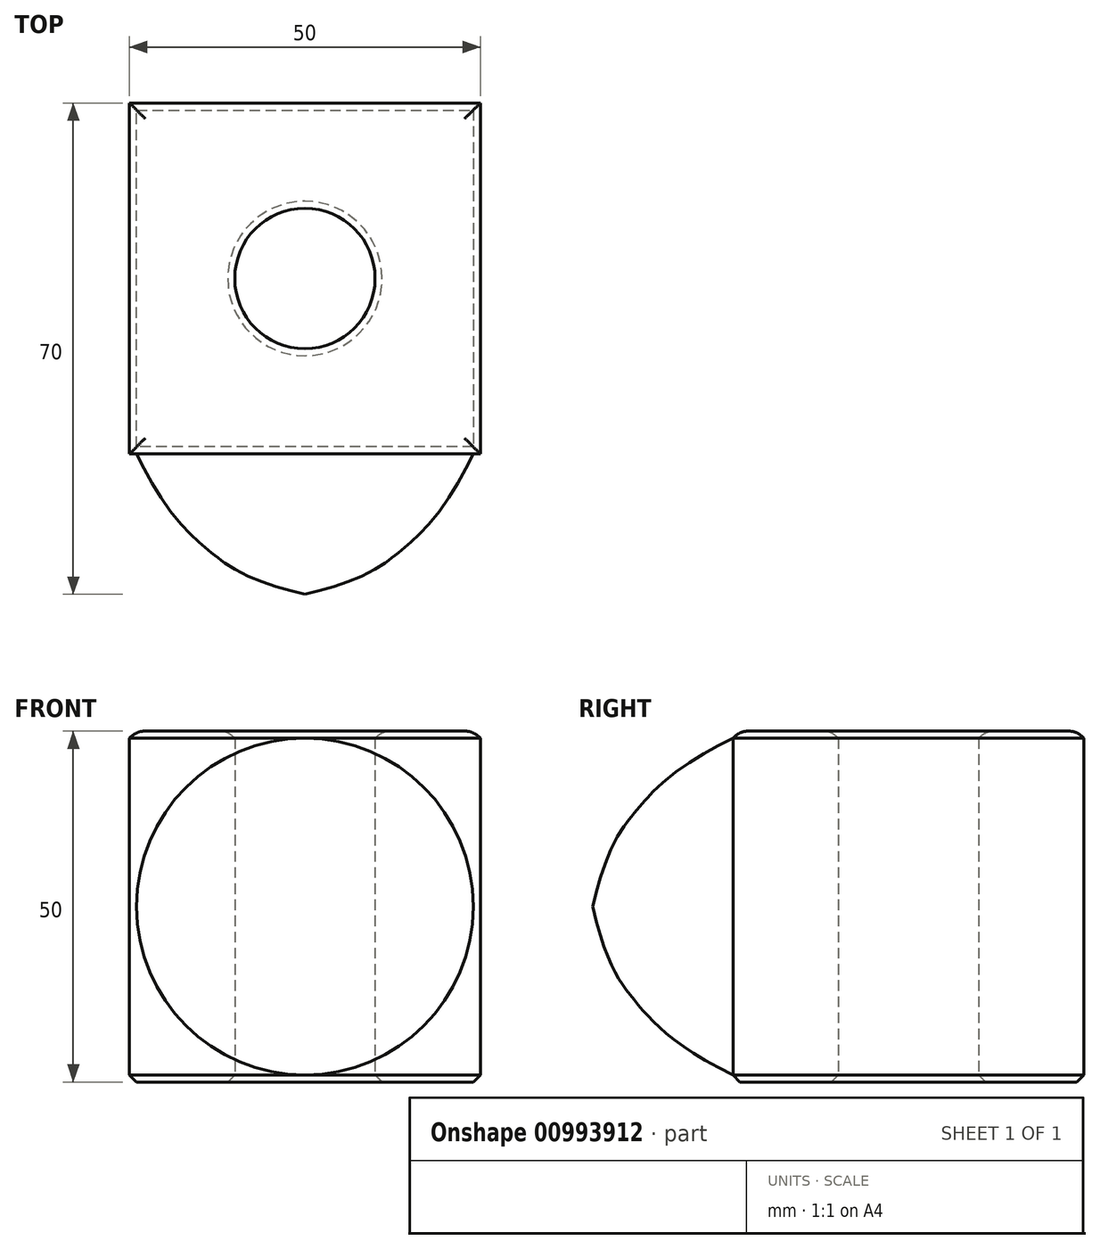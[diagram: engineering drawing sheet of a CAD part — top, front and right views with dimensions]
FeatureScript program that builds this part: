
annotation { "Feature Type Name" : "Feature", "Feature Type Description" : "" }
export const myFeature = defineFeature(function(context is Context, id is Id, definition is map)
    precondition{}
    {
        {
            var Q0;
            Q0=qCreatedBy(makeId("Top.planeOp"),FACE);
            var sketch = newSketch(context, id + "F0", { "sketchPlane" : qUnion([Q0])});
            skLineSegment(sketch, "E0.bottom", {"start": v(25, 25) * mm, "end": v(-25, 25) * mm});
            skLineSegment(sketch, "E0.top", {"start": v(25, -25) * mm, "end": v(-25, -25) * mm});
            skLineSegment(sketch, "E0.left", {"start": v(25, 25) * mm, "end": v(25, -25) * mm});
            skLineSegment(sketch, "E0.right", {"start": v(-25, 25) * mm, "end": v(-25, -25) * mm});
            skPoint(sketch, "E0.middle", {"position": v(0, 0) * mm});
            skSolve(sketch);
        }
        {
            var Q0;
            Q0=makeQuery(id+"F0.imprint","IMPRINT",FACE,{"disambiguationData":[TD([[makeQuery(id+"F0.imprint","IMPRINT",EDGE,{"derivedFrom":sQuery(id+"F0.wireOp",EDGE,"E0.bottom")}),1.0]])]});
            extrude(context, id + "F1", {"entities" : qUnion([Q0]), "depth" : 50 * mm, "offsetDistance" : 25 * mm});
        }
        {
            var Q0;
            Q0=qCreatedBy(makeId("Top.planeOp"),FACE);
            var sketch = newSketch(context, id + "F2", { "sketchPlane" : qUnion([Q0])});
            skCircle(sketch, "E1", {"center": v(0, 0) * mm, "radius": 10 * mm});
            skSolve(sketch);
        }
        {
            var Q0;
            Q0 = qSketchRegion(id + "F2", true);
            var Q1;
            Q1=makeQuery(id+"F1.opExtrude","CAP_FACE",FACE,{"disambiguationData":[OSD([sQuery(id+"F0.wireOp",EDGE,"E0.bottom"),sQuery(id+"F0.wireOp",EDGE,"E0.top"),sQuery(id+"F0.wireOp",EDGE,"E0.left"),sQuery(id+"F0.wireOp",EDGE,"E0.right")])],"isStart":false});
            extrude(context, id + "F3", {"entities" : qUnion([Q0, Q1]), "operationType" : NewBodyOperationType.REMOVE, "endBound" : BoundingType.THROUGH_ALL, "depth" : 20 * mm, "offsetDistance" : 25 * mm});
        }
        {
            var Q0;
            Q0=makeQuery(id+"F1.opExtrude","CAP_FACE",FACE,{"disambiguationData":[OSD([sQuery(id+"F0.wireOp",EDGE,"E0.bottom"),sQuery(id+"F0.wireOp",EDGE,"E0.top"),sQuery(id+"F0.wireOp",EDGE,"E0.left"),sQuery(id+"F0.wireOp",EDGE,"E0.right")])],"isStart":true});
            var Q1;
            Q1=makeQuery(id+"F1.opExtrude","CAP_FACE",FACE,{"disambiguationData":[OSD([sQuery(id+"F0.wireOp",EDGE,"E0.bottom"),sQuery(id+"F0.wireOp",EDGE,"E0.top"),sQuery(id+"F0.wireOp",EDGE,"E0.left"),sQuery(id+"F0.wireOp",EDGE,"E0.right")])],"isStart":false});
            chamfer(context, id + "F4", {"entities" : qUnion([Q0, Q1]), "width" : 1 * mm, "tangentPropagation" : true});
        }
        {
            var Q0;
            Q0=makeQuery(id+"F1.opExtrude","CAP_FACE",FACE,{"disambiguationData":[OSD([sQuery(id+"F0.wireOp",EDGE,"E0.bottom"),sQuery(id+"F0.wireOp",EDGE,"E0.top"),sQuery(id+"F0.wireOp",EDGE,"E0.left"),sQuery(id+"F0.wireOp",EDGE,"E0.right")])],"isStart":false});
            fillet(context, id + "F5", {"entities" : qUnion([Q0]), "radius" : 3 * mm, "tangentPropagation" : true, "rho" : 0.5, "crossSection" : FilletCrossSection.CONIC, "allowEdgeOverflow" : false});
        }
        {
            var Q0;
            Q0=qCreatedBy(makeId("Right.planeOp"),FACE);
            var sketch = newSketch(context, id + "F6", { "sketchPlane" : qUnion([Q0])});
            skLineSegment(sketch, "E2.0", {"start": v(-25, 25) * mm, "end": v(-25, 1) * mm});
            skLineSegment(sketch, "E3", {"start": v(-25, 25) * mm, "end": v(-45, 25) * mm});
            skFitSpline(sketch, "E4", {"points": [v(-45, 25) * mm, v(-39.14, 11.78) * mm, v(-25, 1) * mm], "startDerivative": vector(13, -53.55) * mm, "endDerivative": vector(50.8, -24.84) * mm});
            skPoint(sketch, "E5.orphan", {"position": v(-25, 49) * mm});
            skSolve(sketch);
        }
        {
            var Q0;
            Q0=makeQuery(id+"F6.imprint","IMPRINT",FACE,{"disambiguationData":[TD([[makeQuery(id+"F6.imprint","IMPRINT",EDGE,{"derivedFrom":sQuery(id+"F6.wireOp",EDGE,"E2.0")}),-1.0]])]});
            var Q1;
            Q1=sQuery(id+"F6.wireOp",EDGE,"E3");
            revolve(context, id + "F7", {"surfaceOperationType" : NewSurfaceOperationType.NEW, "entities" : qUnion([Q0]), "axis" : qUnion([Q1]), "revolveType" : RevolveType.FULL});
        }
    });
